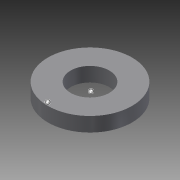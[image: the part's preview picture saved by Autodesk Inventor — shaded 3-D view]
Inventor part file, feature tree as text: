
AUTODESK INVENTOR PART (.ipt)
format: ipt  version: 2015 (Build 190159000, 159)  size: 100,864 bytes
history: native  units: in
note: dims shown in document units (in); Inventor stores cm internally (conversion verified against a paired STEP export)
features: other x2, extrude x1, imported_body x1, sketch x1
ambient origin geometry x8: Origin, YZ Plane, XZ Plane, XY Plane, X Axis, Y Axis, Z Axis, Center Point
bodies: Body1 (feature_tree)
feature tree (5):
  other  "Washer Steel"
  parser-record x1  (decoder bookkeeping rows leaked as tree rows — omitted from the tree; the rows remain in map.json)
  extrude  "Extrusion1"  TaperAngle=0.0deg  [1 undecoded]
  imported_body  "Base1"
  sketch  "Sketch1"  dims[d0=0.0in d1=0.0in d2=0.032in d3=0.0in]
note: 1 required parameter value undecoded (feature->parameter linkage not recoverable at this tier; creation-order binding heuristic only, values carry confidence <= 0.55)
